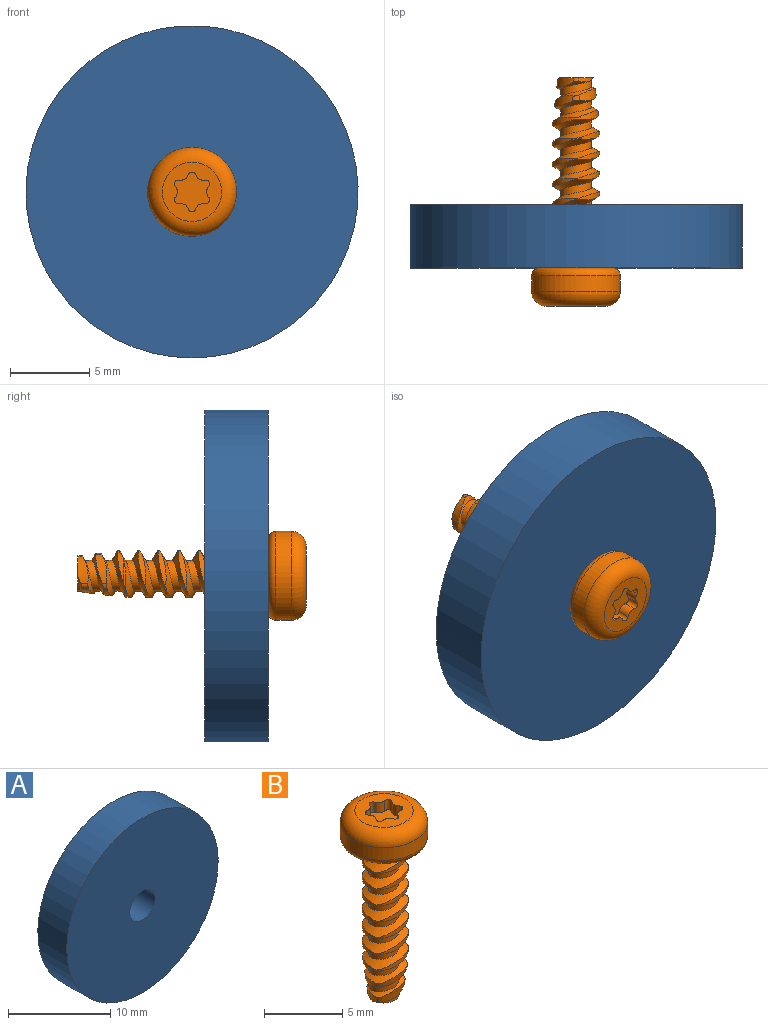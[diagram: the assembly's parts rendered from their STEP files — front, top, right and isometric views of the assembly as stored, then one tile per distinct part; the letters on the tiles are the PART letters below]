
ASSEMBLY  parts=2 mates=1
PART A: 4 faces, bbox 20.9x4x20.9 mm
  f0: cylinder r=1.75mm len=4mm, axis (0,-1,0), area 44mm2, adj f2,f3
  f1: cylinder r=10.46mm len=20.93mm, axis (0,-1,0), area 263mm2, adj f2,f3
  f2: plane 20.93x20.93mm, normal (0,1,0), area 334.4mm2, adj f0,f1
  f3: plane 20.93x20.93mm, normal (0,-1,0), area 334.4mm2, adj f0,f1
PART B: 83 faces, bbox 6.1x6.1x14.8 mm
  f0: plane 4.64x4.64mm, normal (0,0,-1), area 12.5mm2, adj f1,f19,f20,f23,f65
  f1: torus R=2.32mm, axis (0,0,-1), area 12.4mm2, adj f0,f2
  f2: cylinder r=2.8mm len=5.6mm, axis (0,0,-1), area 17.4mm2, adj f1,f3
  f3: torus R=1.87mm, axis (0,0,-1), area 22.7mm2, adj f2,f4
  f4: plane 3.73x3.73mm, normal (0,0,1), area 7.3mm2, adj f3,f5,f6,f7,f9,f10,f11,f12
  f5: cylinder r=0.49mm len=0.8mm, axis (0,0,1), area 0.6mm2, adj f4,f6,f8,f17
  f6: cylinder r=0.25mm len=0.8mm, axis (0,0,1), area 0.5mm2, adj f4,f5,f7,f8
  f7: cylinder r=0.49mm len=0.8mm, axis (0,0,1), area 0.6mm2, adj f4,f6,f8,f9
  f8: plane 2.49x2.22mm, normal (0,0,1), area 3.6mm2, adj f5,f6,f7,f9,f10,f11,f12,f13
  f9: cylinder r=0.25mm len=0.8mm, axis (0,0,1), area 0.5mm2, adj f4,f7,f8,f10
  f10: cylinder r=0.49mm len=0.8mm, axis (0,0,1), area 0.6mm2, adj f4,f8,f9,f11
  f11: cylinder r=0.25mm len=0.8mm, axis (0,0,1), area 0.5mm2, adj f4,f8,f10,f12
  f12: cylinder r=0.49mm len=0.8mm, axis (0,0,1), area 0.6mm2, adj f4,f8,f11,f13
  f13: cylinder r=0.25mm len=0.8mm, axis (0,0,1), area 0.5mm2, adj f4,f8,f12,f14
  f14: cylinder r=0.49mm len=0.8mm, axis (0,0,1), area 0.6mm2, adj f4,f8,f13,f15
  f15: cylinder r=0.25mm len=0.8mm, axis (0,0,1), area 0.5mm2, adj f4,f8,f14,f16
  f16: cylinder r=0.49mm len=0.8mm, axis (0,0,1), area 0.6mm2, adj f4,f8,f15,f17
  f17: cylinder r=0.25mm len=0.8mm, axis (0,0,1), area 0.5mm2, adj f4,f5,f8,f16
  f18: plane 2.24x2.19mm, normal (0,0,-1), area 3.3mm2, adj f19,f20,f23,f67,f69,f73
  f19: bspline ~12.76x3.25mm, area 37.3mm2, adj f0,f18,f21,f22,f23,f24,f25,f26
  f20: bspline ~12.6x3.25mm, area 37.2mm2, adj f0,f18,f21,f23,f24,f25,f26,f27
  f21: cylinder r=0.65mm len=0.56mm, axis (0,0,1), area 0.1mm2, adj f19,f20,f22,f37,f82
  f22: cylinder r=2.32mm len=1.43mm, axis (0,0,1), area 0.1mm2, adj f19,f21,f77
  f23: cylinder r=0.97mm len=12mm, axis (0,0,-1), area 26.1mm2, adj f0,f18,f19,f20
  f24: cylinder r=2.32mm len=2.01mm, axis (0,0,1), area 0.7mm2, adj f19,f20,f30,f57
  f25: cylinder r=2.32mm len=2.01mm, axis (0,0,1), area 0.7mm2, adj f19,f20,f31,f58
  f26: cylinder r=2.32mm len=2.01mm, axis (0,0,1), area 0.7mm2, adj f19,f20,f32,f59
  f27: cylinder r=2.32mm len=2.01mm, axis (0,0,1), area 0.7mm2, adj f19,f20,f33,f60
  f28: cylinder r=2.32mm len=2.01mm, axis (0,0,1), area 0.7mm2, adj f19,f20,f34,f61
  f29: cylinder r=2.32mm len=2.01mm, axis (0,0,1), area 0.7mm2, adj f19,f20,f35,f62
  f30: cylinder r=0.65mm len=0.56mm, axis (0,0,1), area 0.1mm2, adj f19,f20,f24,f37
  f31: cylinder r=0.65mm len=0.56mm, axis (0,0,1), area 0.1mm2, adj f19,f20,f25,f38
  f32: cylinder r=0.65mm len=0.56mm, axis (0,0,1), area 0.1mm2, adj f19,f20,f26,f39
  f33: cylinder r=0.65mm len=0.56mm, axis (0,0,1), area 0.1mm2, adj f19,f20,f27,f40
  f34: cylinder r=0.65mm len=0.56mm, axis (0,0,1), area 0.1mm2, adj f19,f20,f28,f41
  f35: cylinder r=0.65mm len=0.56mm, axis (0,0,1), area 0.1mm2, adj f19,f20,f29,f42
  f36: cylinder r=0.65mm len=0.56mm, axis (0,0,1), area 0.1mm2, adj f19,f20,f43,f64
  f37: cylinder r=2.32mm len=2.32mm, axis (0,0,1), area 0.7mm2, adj f19,f20,f21,f30
  f38: cylinder r=2.32mm len=2.32mm, axis (0,0,1), area 0.7mm2, adj f19,f20,f31,f44
  f39: cylinder r=2.32mm len=2.32mm, axis (0,0,1), area 0.7mm2, adj f19,f20,f32,f45
  f40: cylinder r=2.32mm len=2.32mm, axis (0,0,1), area 0.7mm2, adj f19,f20,f33,f46
  f41: cylinder r=2.32mm len=2.32mm, axis (0,0,1), area 0.7mm2, adj f19,f20,f34,f47
  f42: cylinder r=2.32mm len=2.32mm, axis (0,0,1), area 0.7mm2, adj f19,f20,f35,f48
  f43: cylinder r=2.32mm len=2.32mm, axis (0,0,1), area 0.7mm2, adj f19,f20,f36,f49
  f44: cylinder r=0.65mm len=0.56mm, axis (0,0,1), area 0.1mm2, adj f19,f20,f38,f51
  f45: cylinder r=0.65mm len=0.56mm, axis (0,0,1), area 0.1mm2, adj f19,f20,f39,f52
  f46: cylinder r=0.65mm len=0.56mm, axis (0,0,1), area 0.1mm2, adj f19,f20,f40,f53
  f47: cylinder r=0.65mm len=0.56mm, axis (0,0,1), area 0.1mm2, adj f19,f20,f41,f54
  f48: cylinder r=0.65mm len=0.56mm, axis (0,0,1), area 0.1mm2, adj f19,f20,f42,f55
  f49: cylinder r=0.65mm len=0.56mm, axis (0,0,1), area 0.1mm2, adj f19,f20,f43,f56
  f50: cylinder r=0.65mm len=0.56mm, axis (0,0,1), area 0.1mm2, adj f19,f20,f65,f66
  f51: cylinder r=2.32mm len=2.01mm, axis (0,0,1), area 0.7mm2, adj f19,f20,f44,f57
  f52: cylinder r=2.32mm len=2.01mm, axis (0,0,1), area 0.7mm2, adj f19,f20,f45,f58
  f53: cylinder r=2.32mm len=2.01mm, axis (0,0,1), area 0.7mm2, adj f19,f20,f46,f59
  f54: cylinder r=2.32mm len=2.01mm, axis (0,0,1), area 0.7mm2, adj f19,f20,f47,f60
  f55: cylinder r=2.32mm len=2.01mm, axis (0,0,1), area 0.7mm2, adj f19,f20,f48,f61
  f56: cylinder r=2.32mm len=2.01mm, axis (0,0,1), area 0.7mm2, adj f19,f20,f49,f62
  f57: cylinder r=0.65mm len=0.65mm, axis (0,0,1), area 0.1mm2, adj f19,f20,f24,f51
  f58: cylinder r=0.65mm len=0.65mm, axis (0,0,1), area 0.1mm2, adj f19,f20,f25,f52
  f59: cylinder r=0.65mm len=0.65mm, axis (0,0,1), area 0.1mm2, adj f19,f20,f26,f53
  f60: cylinder r=0.65mm len=0.65mm, axis (0,0,1), area 0.1mm2, adj f19,f20,f27,f54
  f61: cylinder r=0.65mm len=0.65mm, axis (0,0,1), area 0.1mm2, adj f19,f20,f28,f55
  f62: cylinder r=0.65mm len=0.65mm, axis (0,0,1), area 0.1mm2, adj f19,f20,f29,f56
  f63: cylinder r=0.65mm len=0.65mm, axis (0,0,1), area 0.1mm2, adj f19,f20,f64,f66
  f64: cylinder r=2.32mm len=2.01mm, axis (0,0,1), area 0.7mm2, adj f19,f20,f36,f63
  f65: cylinder r=2.32mm len=1.61mm, axis (0,0,1), area 0.2mm2, adj f0,f19,f20,f50
  f66: cylinder r=2.32mm len=2.01mm, axis (0,0,1), area 0.7mm2, adj f19,f20,f50,f63
  f67: cone r=0.65mm half-angle=7deg, axis (0,0,1), area 0.1mm2, adj f18,f19,f69,f73
  f68: cone r=0.65mm half-angle=7deg, axis (0,0,1), area 0.2mm2, adj f19,f20,f70,f74
  f69: cone r=2.32mm half-angle=7deg, axis (0,0,1), area 0.2mm2, adj f18,f19,f67
  f70: cone r=2.32mm half-angle=7deg, axis (0,0,1), area 0.8mm2, adj f19,f20,f68,f71
  f71: cone r=0.65mm half-angle=7deg, axis (0,0,1), area 0.2mm2, adj f19,f20,f70,f72
  f72: cone r=2.32mm half-angle=7deg, axis (0,0,1), area 0.9mm2, adj f19,f20,f71,f75
  f73: cone r=2.32mm half-angle=7deg, axis (0,0,1), area 0.9mm2, adj f18,f19,f20,f67,f75
  f74: cone r=2.32mm half-angle=7deg, axis (0,0,1), area 0.7mm2, adj f19,f20,f68,f76
  f75: cone r=0.65mm half-angle=7deg, axis (0,0,1), area 0.2mm2, adj f19,f20,f72,f73
  f76: cone r=0.65mm half-angle=7deg, axis (0,0,1), area 0.1mm2, adj f19,f20,f74,f81
  f77: cone r=2.32mm half-angle=7deg, axis (0,0,1), area 0.6mm2, adj f19,f20,f22,f78,f82
  f78: cone r=0.65mm half-angle=7deg, axis (0,0,1), area 0.1mm2, adj f19,f20,f77,f79
  f79: cone r=2.32mm half-angle=7deg, axis (0,0,1), area 0.9mm2, adj f19,f20,f78,f80
  f80: cone r=0.65mm half-angle=7deg, axis (0,0,1), area 0.1mm2, adj f19,f20,f79,f81
  f81: cone r=2.32mm half-angle=7deg, axis (0,0,1), area 0.8mm2, adj f19,f20,f76,f80
  f82: cone r=0.65mm half-angle=7deg, axis (0,0,1), area 0mm2, adj f20,f21,f77
PLACE A at identity
PLACE B rot(axis=(1,0,0),90deg) t=(0,35,0)mm
MATE fastened B.f2 <-> A.f0  axis (0,1,0) through (0,35,0)mm
